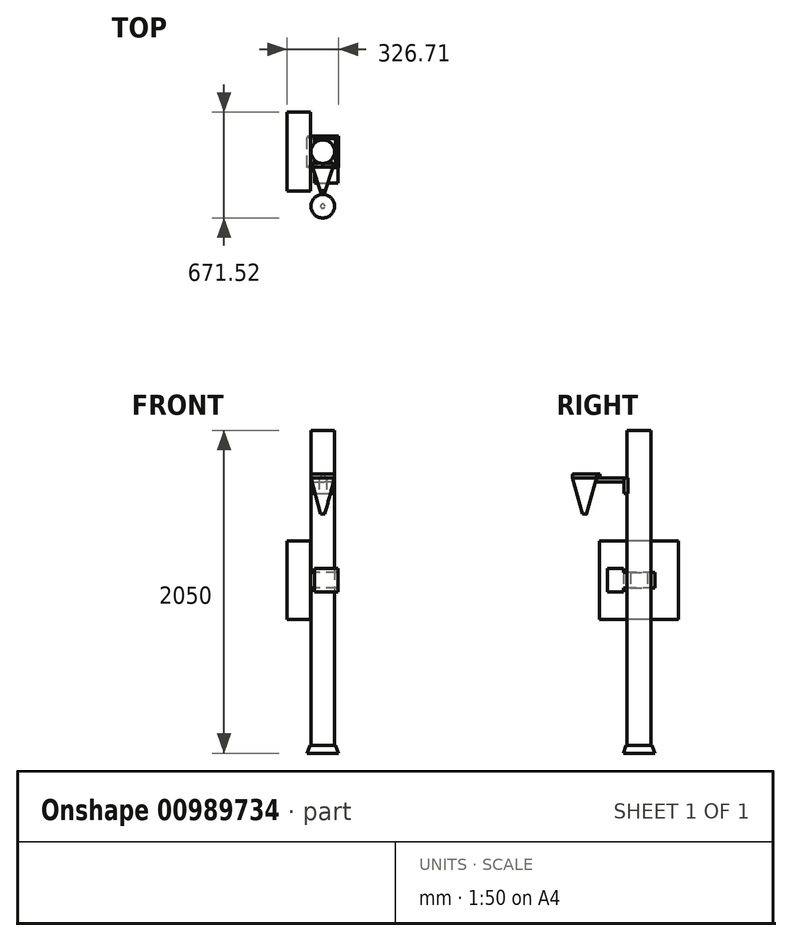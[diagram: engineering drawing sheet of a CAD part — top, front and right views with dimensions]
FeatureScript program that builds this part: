
annotation { "Feature Type Name" : "Feature", "Feature Type Description" : "" }
export const myFeature = defineFeature(function(context is Context, id is Id, definition is map)
    precondition{}
    {
        {
            var Q0;
            Q0=qCreatedBy(makeId("Top.planeOp"),FACE);
            var sketch = newSketch(context, id + "F0", { "sketchPlane" : qUnion([Q0])});
            skLineSegment(sketch, "E0.bottom", {"start": v(-100, 100) * mm, "end": v(100, 100) * mm});
            skLineSegment(sketch, "E0.top", {"start": v(-100, -100) * mm, "end": v(100, -100) * mm});
            skLineSegment(sketch, "E0.left", {"start": v(-100, 100) * mm, "end": v(-100, -100) * mm});
            skLineSegment(sketch, "E0.right", {"start": v(100, 100) * mm, "end": v(100, -100) * mm});
            skLineSegment(sketch, "E1", {"start": v(0, 26.75) * mm, "end": v(0, -21.17) * mm, "construction": true});
            skLineSegment(sketch, "E2", {"start": v(-21.5, 0) * mm, "end": v(23.8, 0) * mm, "construction": true});
            skSolve(sketch);
        }
        {
            var Q0;
            Q0 = qSketchRegion(id + "F0", true);
            extrude(context, id + "F1", {"entities" : qUnion([Q0]), "depth" : 50 * mm, "offsetDistance" : 25.4 * mm, "hasDraft" : true, "draftAngle" : 20 * degree, "draftPullDirection" : true});
        }
        {
            var Q0;
            Q0=makeQuery(id+"F1.opExtrude","CAP_FACE",FACE,{"disambiguationData":[OSD([sQuery(id+"F0.wireOp",EDGE,"E0.bottom"),sQuery(id+"F0.wireOp",EDGE,"E0.top"),sQuery(id+"F0.wireOp",EDGE,"E0.left"),sQuery(id+"F0.wireOp",EDGE,"E0.right")])],"isStart":false});
            var sketch = newSketch(context, id + "F2", { "sketchPlane" : qUnion([Q0])});
            skCircle(sketch, "E3", {"center": v(0, 0) * mm, "radius": 75 * mm});
            skSolve(sketch);
        }
        {
            var Q0;
            Q0 = qSketchRegion(id + "F2", true);
            extrude(context, id + "F3", {"entities" : qUnion([Q0]), "operationType" : NewBodyOperationType.ADD, "depth" : 2000 * mm, "offsetDistance" : 25.4 * mm});
        }
        {
            var Q0;
            Q0=qCreatedBy(makeId("Right.planeOp"),FACE);
            cPlane(context, id + "F4", {"entities" : qUnion([Q0]), "cplaneType" : CPlaneType.OFFSET, "offset" : 76.7 * mm, "oppositeDirection" : true, "width" : 152.4 * mm, "height" : 152.4 * mm});
        }
        {
            var Q0;
            Q0=qCreatedBy(id+"F4.planeOp",FACE);
            var sketch = newSketch(context, id + "F5", { "sketchPlane" : qUnion([Q0])});
            skLineSegment(sketch, "E4.bottom", {"start": v(100, 1150) * mm, "end": v(-100, 1150) * mm});
            skLineSegment(sketch, "E4.top", {"start": v(100, 1050) * mm, "end": v(-100, 1050) * mm});
            skLineSegment(sketch, "E4.left", {"start": v(100, 1150) * mm, "end": v(100, 1050) * mm});
            skLineSegment(sketch, "E4.right", {"start": v(-100, 1150) * mm, "end": v(-100, 1050) * mm});
            skLineSegment(sketch, "E5", {"start": v(0, 267.8) * mm, "end": v(0, 1066.8) * mm, "construction": true});
            skSolve(sketch);
        }
        {
            var Q0;
            Q0 = qSketchRegion(id + "F5", true);
            extrude(context, id + "F6", {"entities" : qUnion([Q0]), "operationType" : NewBodyOperationType.ADD, "depth" : 25.4 * mm, "offsetDistance" : 25.4 * mm});
        }
        {
            var Q0;
            Q0=makeQuery(id+"F6.opExtrude","CAP_FACE",FACE,{"disambiguationData":[OSD([sQuery(id+"F5.wireOp",EDGE,"E4.bottom"),sQuery(id+"F5.wireOp",EDGE,"E4.top"),sQuery(id+"F5.wireOp",EDGE,"E4.left"),sQuery(id+"F5.wireOp",EDGE,"E4.right")])],"isStart":true});
            var sketch = newSketch(context, id + "F7", { "sketchPlane" : qUnion([Q0])});
            skLineSegment(sketch, "E6", {"start": v(0, 1486.8) * mm, "end": v(0, 812.23) * mm, "construction": true});
            skPoint(sketch, "E6.endSnap0", {"position": v(0, 1150) * mm});
            skLineSegment(sketch, "E7", {"start": v(-222.85, 1100) * mm, "end": v(254.97, 1100) * mm, "construction": true});
            skPoint(sketch, "E7.startSnap0", {"position": v(-100, 1100) * mm});
            skLineSegment(sketch, "E8.bottom", {"start": v(-250, 1350) * mm, "end": v(250, 1350) * mm});
            skLineSegment(sketch, "E8.top", {"start": v(-250, 850) * mm, "end": v(250, 850) * mm});
            skLineSegment(sketch, "E8.left", {"start": v(-250, 1350) * mm, "end": v(-250, 850) * mm});
            skLineSegment(sketch, "E8.right", {"start": v(250, 1350) * mm, "end": v(250, 850) * mm});
            skSolve(sketch);
        }
        {
            var Q0;
            Q0 = qSketchRegion(id + "F7", true);
            extrude(context, id + "F8", {"entities" : qUnion([Q0]), "operationType" : NewBodyOperationType.ADD, "depth" : 150 * mm, "offsetDistance" : 25.4 * mm});
        }
        {
            var Q0;
            {var subQ0=sQuery(id+"F5.wireOp",EDGE,"E4.bottom");var subQ1=sQuery(id+"F5.wireOp",EDGE,"E4.right");var subQ2=sQuery(id+"F5.wireOp",EDGE,"E4.top");Q0=makeQuery(id+"F6.boolean.opBoolean","SPLIT",FACE,{"disambiguationData":[TD([makeQuery(id+"F6.opExtrude","SWEPT_FACE",FACE,{"disambiguationData":[OSD([subQ1])]})])],"derivedFrom":makeQuery(id+"F6.opExtrude","CAP_FACE",FACE,{"disambiguationData":[OSD([subQ0,subQ2,sQuery(id+"F5.wireOp",EDGE,"E4.left"),subQ1])],"isStart":false})});}
            var sketch = newSketch(context, id + "F9", { "sketchPlane" : qUnion([Q0])});
            skLineSegment(sketch, "E9.bottom", {"start": v(-77.35, 1050) * mm, "end": v(-100, 1050) * mm});
            skLineSegment(sketch, "E9.top", {"start": v(-77.35, 1150) * mm, "end": v(-100, 1150) * mm});
            skLineSegment(sketch, "E9.left", {"start": v(-77.35, 1050) * mm, "end": v(-77.35, 1150) * mm});
            skLineSegment(sketch, "E9.right", {"start": v(-100, 1050) * mm, "end": v(-100, 1150) * mm});
            skSolve(sketch);
        }
        {
            var Q0;
            Q0 = qSketchRegion(id + "F9", true);
            extrude(context, id + "F10", {"entities" : qUnion([Q0]), "operationType" : NewBodyOperationType.ADD, "depth" : 147.32 * mm, "offsetDistance" : 25.4 * mm});
        }
        {
            var Q0;
            Q0=makeQuery(id+"F10.boolean.opBoolean","MERGE",FACE,{"derivedFrom":[makeQuery(id+"F6.opExtrude","SWEPT_FACE",FACE,{"disambiguationData":[OSD([sQuery(id+"F5.wireOp",EDGE,"E4.right")])]}),makeQuery(id+"F10.opExtrude","SWEPT_FACE",FACE,{"disambiguationData":[OSD([sQuery(id+"F9.wireOp",EDGE,"E9.right")])]})]});
            var sketch = newSketch(context, id + "F11", { "sketchPlane" : qUnion([Q0])});
            skLineSegment(sketch, "E10.bottom", {"start": v(-53.99, 1175) * mm, "end": v(96.01, 1175) * mm});
            skLineSegment(sketch, "E10.top", {"start": v(-53.99, 1025) * mm, "end": v(96.01, 1025) * mm});
            skLineSegment(sketch, "E10.left", {"start": v(-53.99, 1175) * mm, "end": v(-53.99, 1025) * mm});
            skLineSegment(sketch, "E10.right", {"start": v(96.01, 1175) * mm, "end": v(96.01, 1025) * mm});
            skLineSegment(sketch, "E11", {"start": v(470.2, 1100) * mm, "end": v(57.17, 1100) * mm, "construction": true});
            skPoint(sketch, "E11.startSnap0", {"position": v(96.01, 1100) * mm});
            skSolve(sketch);
        }
        {
            var Q0;
            Q0 = qSketchRegion(id + "F11", true);
            extrude(context, id + "F12", {"entities" : qUnion([Q0]), "operationType" : NewBodyOperationType.ADD, "depth" : 100 * mm, "offsetDistance" : 25.4 * mm});
        }
        {
            var Q0;
            Q0=qCreatedBy(makeId("Front.planeOp"),FACE);
            cPlane(context, id + "F13", {"entities" : qUnion([Q0]), "cplaneType" : CPlaneType.OFFSET, "offset" : 71.12 * mm, "width" : 152.4 * mm, "height" : 152.4 * mm});
        }
        {
            var Q0;
            Q0=qCreatedBy(id+"F13.planeOp",FACE);
            var sketch = newSketch(context, id + "F14", { "sketchPlane" : qUnion([Q0])});
            skLineSegment(sketch, "E12.bottom", {"start": v(-64.3, 1750) * mm, "end": v(64.3, 1750) * mm});
            skLineSegment(sketch, "E12.top", {"start": v(-64.3, 1650) * mm, "end": v(64.3, 1650) * mm});
            skLineSegment(sketch, "E12.left", {"start": v(-64.3, 1750) * mm, "end": v(-64.3, 1650) * mm});
            skLineSegment(sketch, "E12.right", {"start": v(64.3, 1750) * mm, "end": v(64.3, 1650) * mm});
            skLineSegment(sketch, "E13", {"start": v(0, 1610) * mm, "end": v(0, 1340.01) * mm, "construction": true});
            skSolve(sketch);
        }
        {
            var Q0;
            Q0 = qSketchRegion(id + "F14", true);
            extrude(context, id + "F15", {"entities" : qUnion([Q0]), "operationType" : NewBodyOperationType.ADD, "depth" : 25.4 * mm, "offsetDistance" : 25.4 * mm});
        }
        {
            var Q0;
            Q0=makeQuery(id+"F15.opExtrude","SWEPT_FACE",FACE,{"disambiguationData":[OSD([sQuery(id+"F14.wireOp",EDGE,"E12.bottom")])]});
            var sketch = newSketch(context, id + "F16", { "sketchPlane" : qUnion([Q0])});
            skCircle(sketch, "E14", {"center": v(0, -346.52) * mm, "radius": 75 * mm});
            skSolve(sketch);
        }
        {
            var Q0;
            Q0 = qSketchRegion(id + "F16", true);
            extrude(context, id + "F17", {"entities" : qUnion([Q0]), "depth" : 25.4 * mm, "offsetDistance" : 25.4 * mm, "hasSecondDirection" : true, "secondDirectionOppositeDirection" : true, "secondDirectionDepth" : 231.14 * mm, "hasSecondDirectionDraft" : true, "secondDirectionDraftAngle" : 15 * degree, "secondDirectionDraftPullDirection" : true});
        }
        {
            var Q0;
            Q0=makeQuery(id+"F15.opExtrude","SWEPT_FACE",FACE,{"disambiguationData":[OSD([sQuery(id+"F14.wireOp",EDGE,"E12.bottom")])]});
            var sketch = newSketch(context, id + "F18", { "sketchPlane" : qUnion([Q0])});
            skCircle(sketch, "E15", {"center": v(0, -259.02) * mm, "radius": 12.5 * mm});
            skSolve(sketch);
        }
        {
            var Q0;
            Q0 = qSketchRegion(id + "F18", true);
            extrude(context, id + "F19", {"entities" : qUnion([Q0]), "operationType" : NewBodyOperationType.ADD, "depth" : 25.4 * mm, "offsetDistance" : 25.4 * mm});
        }
        {
            var Q0;
            Q0=makeQuery(id+"F15.opExtrude","SWEPT_FACE",FACE,{"disambiguationData":[OSD([sQuery(id+"F14.wireOp",EDGE,"E12.bottom")])]});
            var sketch = newSketch(context, id + "F20", { "sketchPlane" : qUnion([Q0])});
            skLineSegment(sketch, "E16", {"start": v(-64.3, -96.52) * mm, "end": v(-11.92, -262.78) * mm});
            skLineSegment(sketch, "E17", {"start": v(64.3, -96.52) * mm, "end": v(11.92, -262.78) * mm});
            skArc(sketch, "E18", {"start": v(-11.92, -262.78) * mm, "mid": v(0, -271.52) * mm, "end": v(11.92, -262.78) * mm});
            skLineSegment(sketch, "E19", {"start": v(64.3, -96.52) * mm, "end": v(-64.3, -96.52) * mm});
            skSolve(sketch);
        }
        {
            var Q0;
            Q0=makeQuery(id+"F20.imprint","IMPRINT",FACE,{"disambiguationData":[TD([[makeQuery(id+"F20.imprint","IMPRINT",EDGE,{"derivedFrom":sQuery(id+"F20.wireOp",EDGE,"E16")}),1.0]])]});
            extrude(context, id + "F21", {"entities" : qUnion([Q0]), "oppositeDirection" : true, "depth" : 25.4 * mm, "offsetDistance" : 25.4 * mm});
        }
    });
